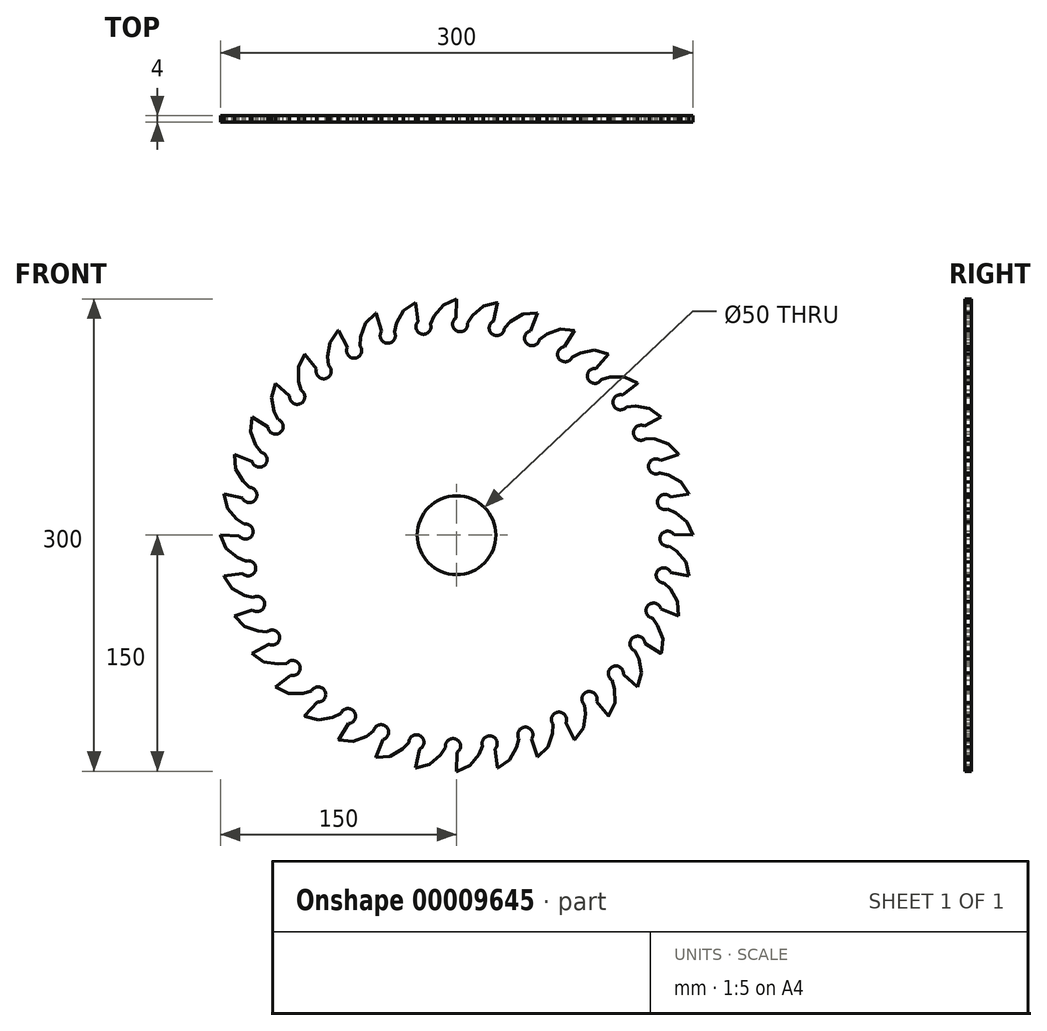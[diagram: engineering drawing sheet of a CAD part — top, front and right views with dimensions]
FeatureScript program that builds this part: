
annotation { "Feature Type Name" : "Feature", "Feature Type Description" : "" }
export const myFeature = defineFeature(function(context is Context, id is Id, definition is map)
    precondition{}
    {
        {
            var Q0;
            Q0=qCreatedBy(makeId("Front.planeOp"),FACE);
            var sketch = newSketch(context, id + "F0", { "sketchPlane" : qUnion([Q0])});
            skArc(sketch, "E0", {"start": v(0, 150) * mm, "mid": v(-13, -149.44) * mm, "end": v(25.9, 147.75) * mm});
            skLineSegment(sketch, "E1", {"start": v(0, 0) * mm, "end": v(0, 182.22) * mm, "construction": true});
            skLineSegment(sketch, "E2", {"start": v(0, 150) * mm, "end": v(-0.4, 138) * mm});
            skArc(sketch, "E3", {"start": v(-0.4, 138) * mm, "mid": v(0.39, 129.58) * mm, "end": v(7, 134.85) * mm});
            skLineSegment(sketch, "E4", {"start": v(7, 134.85) * mm, "end": v(10.19, 139.61) * mm});
            skLineSegment(sketch, "E5", {"start": v(10.19, 139.61) * mm, "end": v(17.1, 145.56) * mm});
            skLineSegment(sketch, "E6", {"start": v(17.1, 145.56) * mm, "end": v(25.9, 147.75) * mm});
            skSolve(sketch);
        }
        {
            var Q0;
            Q0=qSketchRegion(id+"F0",true);
            extrude(context, id + "F1", {"entities" : qUnion([Q0]), "depth" : 4 * mm});
        }
        {
            var Q0;
            Q0=makeQuery(id+"F1.opExtrude","SWEPT_FACE",FACE,{"disambiguationData":[OSD([sQuery(id+"F0.wireOp",EDGE,"E6")])]});
            var Q1;
            Q1=makeQuery(id+"F1.opExtrude","SWEPT_FACE",FACE,{"disambiguationData":[OSD([sQuery(id+"F0.wireOp",EDGE,"E5")])]});
            var Q2;
            Q2=makeQuery(id+"F1.opExtrude","SWEPT_FACE",FACE,{"disambiguationData":[OSD([sQuery(id+"F0.wireOp",EDGE,"E4")])]});
            var Q3;
            Q3=makeQuery(id+"F1.opExtrude","SWEPT_FACE",FACE,{"disambiguationData":[OSD([sQuery(id+"F0.wireOp",EDGE,"E3")])]});
            var Q4;
            Q4=makeQuery(id+"F1.opExtrude","SWEPT_FACE",FACE,{"disambiguationData":[OSD([sQuery(id+"F0.wireOp",EDGE,"E2")])]});
            var Q5;
            Q5=makeQuery(id+"F1.opExtrude","SWEPT_FACE",FACE,{"disambiguationData":[OSD([sQuery(id+"F0.wireOp",EDGE,"E0")])]});
            circularPattern(context, id + "F2", {"faces" : qUnion([Q0, Q1, Q2, Q3, Q4]), "axis" : qUnion([Q5]), "angle" : 10 * degree, "instanceCount" : round(36), "oppositeDirection" : true, "patternType" : PatternType.FACE});
        }
        {
            var Q0;
            Q0=makeQuery(id+"F1.opExtrude","CAP_FACE",FACE,{"disambiguationData":[OSD([sQuery(id+"F0.wireOp",EDGE,"E0"),sQuery(id+"F0.wireOp",EDGE,"E2"),sQuery(id+"F0.wireOp",EDGE,"E3"),sQuery(id+"F0.wireOp",EDGE,"E4"),sQuery(id+"F0.wireOp",EDGE,"E5"),sQuery(id+"F0.wireOp",EDGE,"E6")])],"isStart":false});
            var sketch = newSketch(context, id + "F3", { "sketchPlane" : qUnion([Q0])});
            skCircle(sketch, "E7", {"center": v(0, 0) * mm, "radius": 25 * mm});
            skSolve(sketch);
        }
        {
            var Q0;
            Q0=qSketchRegion(id+"F3",true);
            extrude(context, id + "F4", {"entities" : qUnion([Q0]), "operationType" : NewBodyOperationType.REMOVE, "endBound" : BoundingType.THROUGH_ALL, "oppositeDirection" : true, "depth" : 25 * mm});
        }
    });
